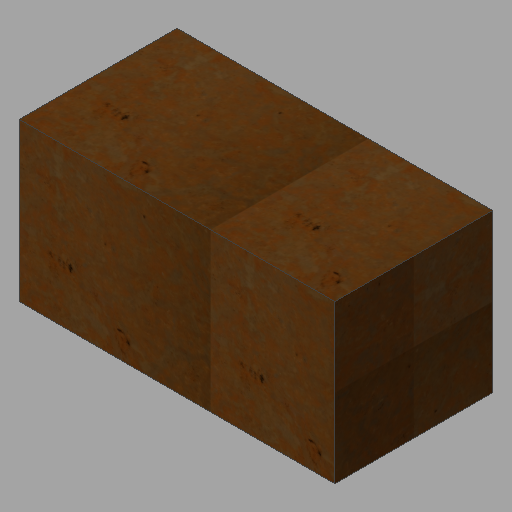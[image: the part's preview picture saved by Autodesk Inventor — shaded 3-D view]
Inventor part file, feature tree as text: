
AUTODESK INVENTOR PART (.ipt)
format: ipt  version: 2023 (Build 270158030, 158C)  size: 324,608 bytes
history: native  units: in
note: dims shown in document units (in); Inventor stores cm internally (conversion verified against a paired STEP export)
features: other x1, extrude x1, sketch x1
ambient origin geometry x8: Origin, YZ Plane, XZ Plane, XY Plane, X Axis, Y Axis, Z Axis, Center Point
bodies: Solid1 (feature_tree)
feature tree (3):
  other  "block"
  extrude  "Extrusion1"  Depth=24.0in
  sketch  "Sketch1"  dims[d0=24.0in d1=24.0in d2=48.0in d3=0.0in]
